# Revit family: HumiPump 3
name_source: partatom
category: Оборудование
units: mm (PartAtom-declared; Revit-internal decimal feet)

## family parameters
Всегда вертикально = Да
Классификация = Нет
На основе рабочей плоскости = Нет
Общий = Нет
При загрузке вырезать с полостями = Нет
Размер круглого соединителя = Использовать диаметр
Тип детали = Нормальный
Точка расчета площади = Нет

## types (1)
- Humi Pump 3
    ADSK_Завод-изготовитель = ООО "Турков"
    ADSK_Количество = 1
    ADSK_Количество фаз = 1
    ADSK_Марка = Humi Pump 3
    ADSK_Масса = 0
    ADSK_Наименование = Адиабатический увлажнитель. Аппаратный модуль Humi Pump 3
    ADSK_Напряжение = 0 В
    ADSK_Полная мощность = 0 В·А
    ADSK_Расход воздуха = 0.0 л/с
    ADSK_Расход жидкости = 0.0 л/с
    ADSK_Ток = 0 А
    A_толщина = 230 мм
    DN = 200 мм
    s1 = 103 мм
    s2 = 56 мм
    s3 = 30 мм
    s4 = 65 мм
    В_ширина = 429 мм
    Высота_КА = 100 мм
    Длина дренажн патр = 50 мм
    Длина патр аппаратн в увлажн = 65 мм
    Длина патрубка подвода чв в апп = 150 мм
    Дренаж = 40 мм
    Подвод из аппартн = 13 мм
    С_высота = 416 мм
    СЗ КА = 200 мм
    СЗ корпуса = 300 мм
    Толщина_КА = 124 мм
    Толщина_листа = 33 мм
    УГО = 1 мм
    Чистая в аппарт = 6 мм
    Ширина_КА = 185 мм
